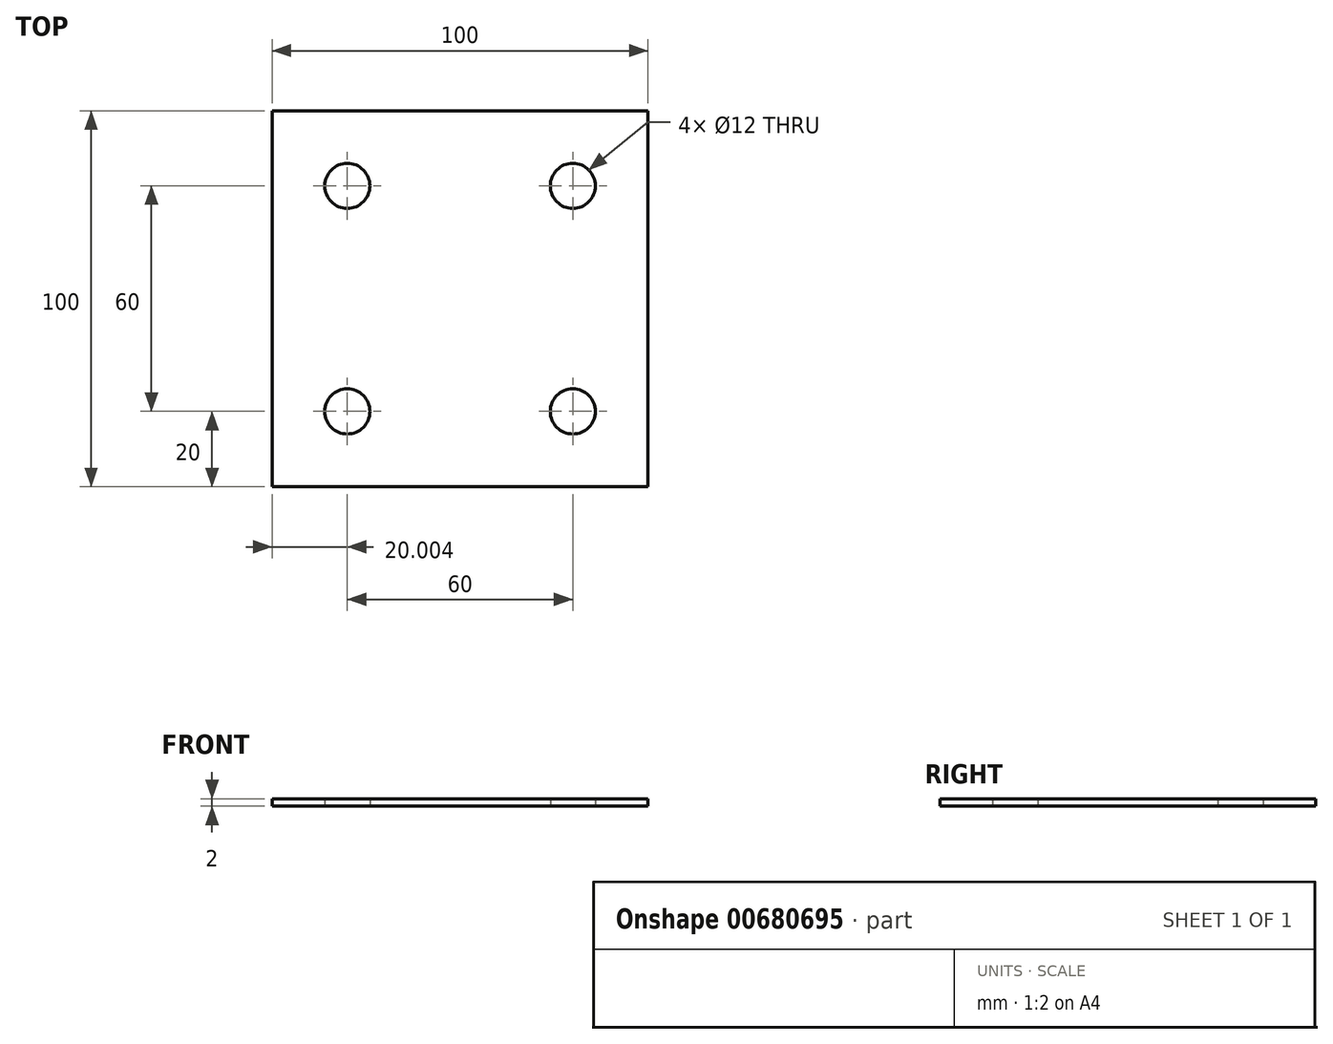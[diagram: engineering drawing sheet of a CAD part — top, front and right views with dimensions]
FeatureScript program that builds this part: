
annotation { "Feature Type Name" : "Feature", "Feature Type Description" : "" }
export const myFeature = defineFeature(function(context is Context, id is Id, definition is map)
    precondition{}
    {
        {
            var Q0;
            Q0=qCreatedBy(makeId("Top.planeOp"),FACE);
            var sketch = newSketch(context, id + "F0", { "sketchPlane" : qUnion([Q0])});
            skLineSegment(sketch, "E0.bottom", {"start": v(52.1, 50) * mm, "end": v(-47.9, 50) * mm});
            skLineSegment(sketch, "E0.top", {"start": v(52.1, -50) * mm, "end": v(-47.9, -50) * mm});
            skLineSegment(sketch, "E0.left", {"start": v(52.1, 50) * mm, "end": v(52.1, -50) * mm});
            skLineSegment(sketch, "E0.right", {"start": v(-47.9, 50) * mm, "end": v(-47.9, -50) * mm});
            skPoint(sketch, "E0.middle", {"position": v(2.1, 0) * mm});
            skCircle(sketch, "E1", {"center": v(-27.9, 30) * mm, "radius": 6 * mm});
            skCircle(sketch, "E2", {"center": v(32.1, 30) * mm, "radius": 6 * mm});
            skCircle(sketch, "E3", {"center": v(-27.9, -30) * mm, "radius": 6 * mm});
            skCircle(sketch, "E4", {"center": v(32.1, -30) * mm, "radius": 6 * mm});
            skSolve(sketch);
        }
        {
            var Q0;
            Q0=makeQuery(id+"F0.imprint","IMPRINT",FACE,{"disambiguationData":[TD([[makeQuery(id+"F0.imprint","IMPRINT",EDGE,{"derivedFrom":sQuery(id+"F0.wireOp",EDGE,"E0.bottom")}),1.0]])]});
            extrude(context, id + "F1", {"entities" : qUnion([Q0]), "depth" : 2 * mm, "offsetDistance" : 25 * mm});
        }
    });
